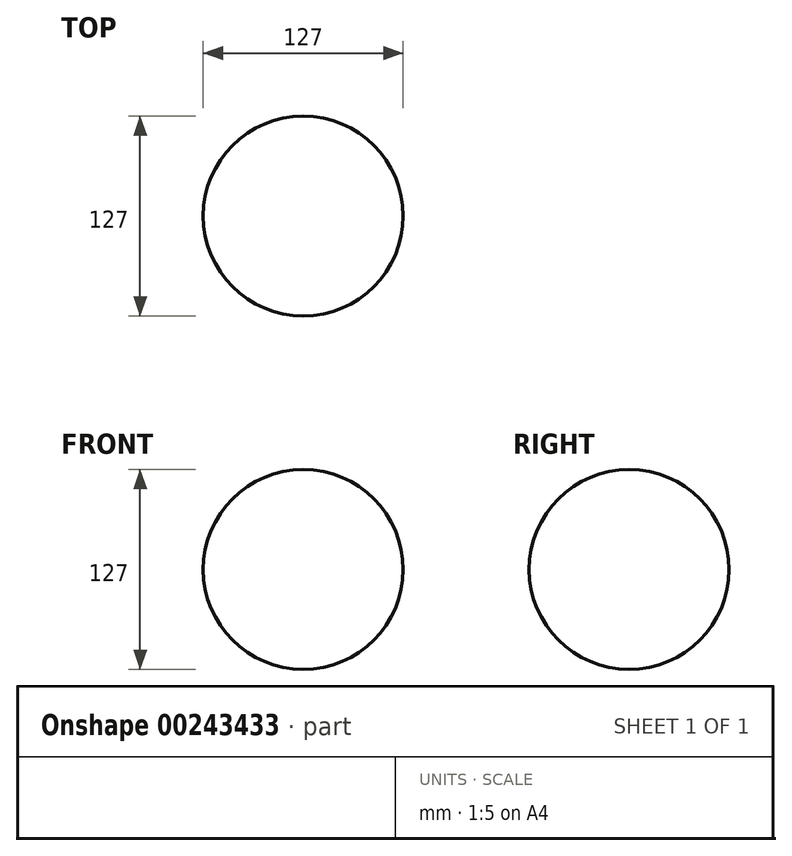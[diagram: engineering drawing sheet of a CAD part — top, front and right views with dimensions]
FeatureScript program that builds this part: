
annotation { "Feature Type Name" : "Feature", "Feature Type Description" : "" }
export const myFeature = defineFeature(function(context is Context, id is Id, definition is map)
    precondition{}
    {
        {
            var Q0;
            Q0=qCreatedBy(makeId("Front.planeOp"),FACE);
            var sketch = newSketch(context, id + "F0", { "sketchPlane" : qUnion([Q0])});
            skLineSegment(sketch, "E0", {"start": v(0, 63.5) * mm, "end": v(0, -63.5) * mm});
            skArc(sketch, "E1", {"start": v(0, -63.5) * mm, "mid": v(63.5, 0) * mm, "end": v(0, 63.5) * mm});
            skSolve(sketch);
        }
        {
            var Q0;
            Q0=makeQuery(id+"F0.imprint","IMPRINT",FACE,{"disambiguationData":[TD([[makeQuery(id+"F0.imprint","IMPRINT",EDGE,{"derivedFrom":sQuery(id+"F0.wireOp",EDGE,"E0")}),1.0]])]});
            var Q1;
            Q1=sQuery(id+"F0.wireOp",EDGE,"E0");
            revolve(context, id + "F1", {"entities" : qUnion([Q0]), "axis" : qUnion([Q1]), "revolveType" : RevolveType.FULL});
        }
    });
